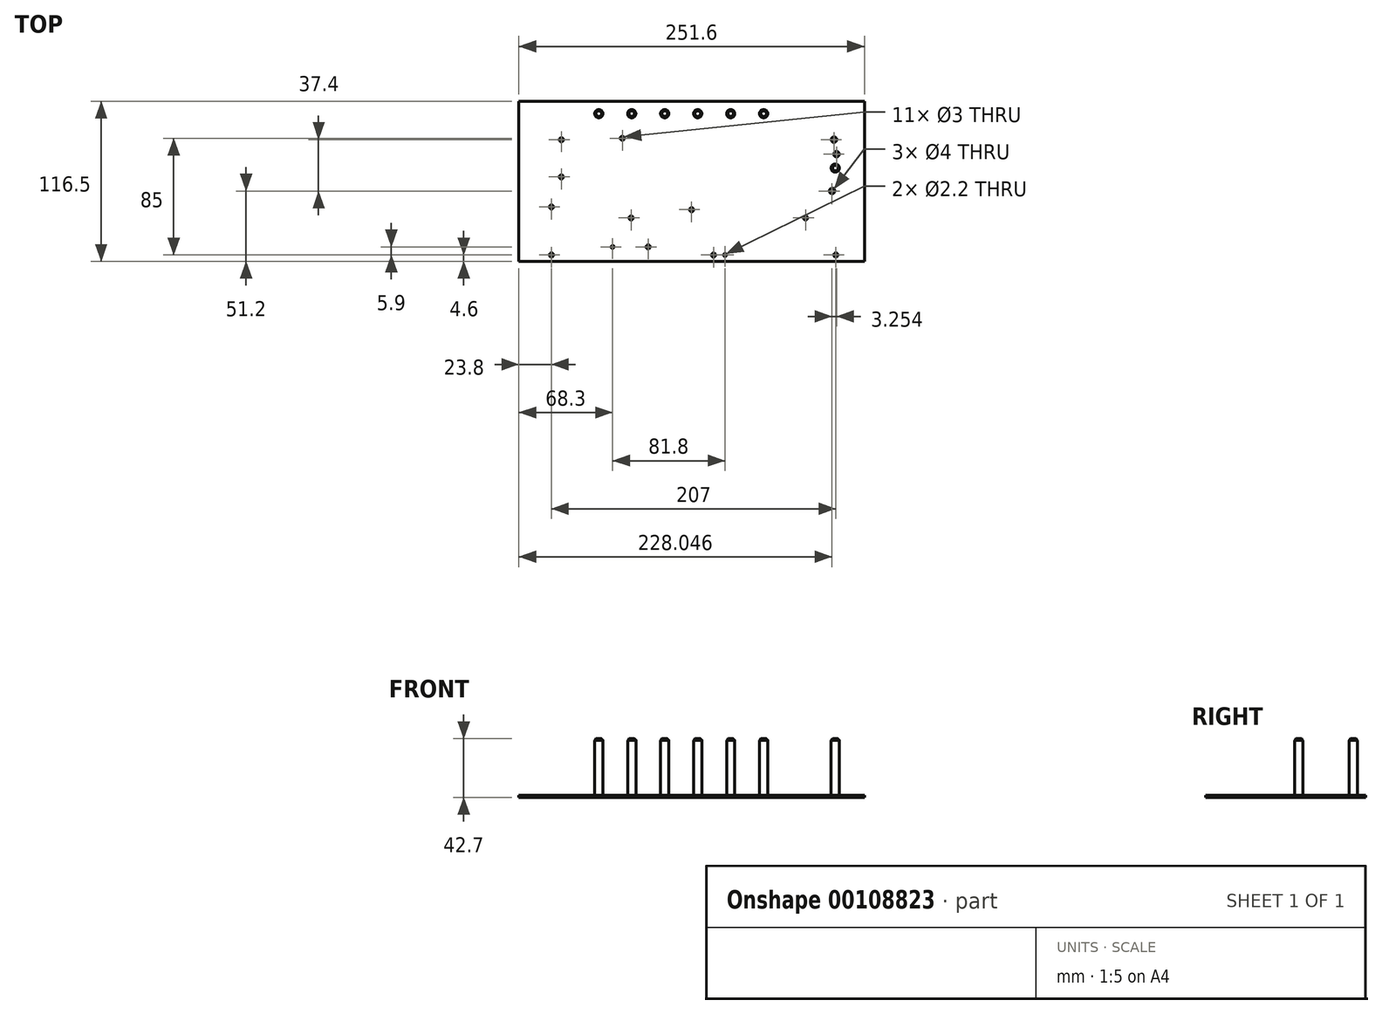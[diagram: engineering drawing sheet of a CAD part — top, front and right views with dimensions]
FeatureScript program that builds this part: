
annotation { "Feature Type Name" : "Feature", "Feature Type Description" : "" }
export const myFeature = defineFeature(function(context is Context, id is Id, definition is map)
    precondition{}
    {
        {
            var Q0;
            Q0=qCreatedBy(makeId("Top.planeOp"),FACE);
            var sketch = newSketch(context, id + "F0", { "sketchPlane" : qUnion([Q0])});
            skLineSegment(sketch, "E0.bottom", {"start": v(0, 0) * mm, "end": v(251.6, 0) * mm});
            skLineSegment(sketch, "E0.top", {"start": v(0, 116.5) * mm, "end": v(251.6, 116.5) * mm});
            skLineSegment(sketch, "E0.left", {"start": v(0, 0) * mm, "end": v(0, 116.5) * mm});
            skLineSegment(sketch, "E0.right", {"start": v(251.6, 0) * mm, "end": v(251.6, 116.5) * mm});
            skLineSegment(sketch, "E1", {"start": v(0, 4.6) * mm, "end": v(251.6, 4.6) * mm, "construction": true});
            skLineSegment(sketch, "E2", {"start": v(23.8, 0) * mm, "end": v(23.8, 116.5) * mm, "construction": true});
            skCircle(sketch, "E3", {"center": v(23.8, 4.6) * mm, "radius": 1.5 * mm});
            skLineSegment(sketch, "E4", {"start": v(0, 39.6) * mm, "end": v(251.6, 39.6) * mm, "construction": true});
            skCircle(sketch, "E5", {"center": v(23.8, 39.6) * mm, "radius": 1.5 * mm});
            skLineSegment(sketch, "E6", {"start": v(0, 31.6) * mm, "end": v(251.6, 31.6) * mm, "construction": true});
            skCircle(sketch, "E7", {"center": v(81.8, 31.6) * mm, "radius": 1.5 * mm});
            skCircle(sketch, "E8", {"center": v(208.8, 31.6) * mm, "radius": 1.5 * mm});
            skCircle(sketch, "E9", {"center": v(141.8, 4.6) * mm, "radius": 1.5 * mm});
            skCircle(sketch, "E10", {"center": v(150.1, 4.6) * mm, "radius": 1.1 * mm});
            skCircle(sketch, "E11", {"center": v(230.8, 4.6) * mm, "radius": 1.5 * mm});
            skCircle(sketch, "E12", {"center": v(125.8, 37.6) * mm, "radius": 1.5 * mm});
            skLineSegment(sketch, "E13", {"start": v(31, 0) * mm, "end": v(31, 116.5) * mm, "construction": true});
            skCircle(sketch, "E14", {"center": v(31, 61.5) * mm, "radius": 1.5 * mm});
            skCircle(sketch, "E15", {"center": v(31, 88.5) * mm, "radius": 1.5 * mm});
            skLineSegment(sketch, "E16", {"start": v(0, 10.5) * mm, "end": v(251.6, 10.5) * mm, "construction": true});
            skCircle(sketch, "E17", {"center": v(68.3, 10.5) * mm, "radius": 1.1 * mm});
            skCircle(sketch, "E18", {"center": v(94.2, 10.5) * mm, "radius": 1.5 * mm});
            skCircle(sketch, "E19", {"center": v(75.4, 89.6) * mm, "radius": 1.5 * mm});
            skCircle(sketch, "E20", {"center": v(228.05, 51.2) * mm, "radius": 2 * mm});
            skCircle(sketch, "E21", {"center": v(231.3, 78) * mm, "radius": 2 * mm});
            skCircle(sketch, "E22", {"center": v(229.5, 88.6) * mm, "radius": 2 * mm});
            skSolve(sketch);
        }
        {
            var Q0;
            Q0=makeQuery(id+"F0.imprint","IMPRINT",FACE,{"disambiguationData":[TD([[makeQuery(id+"F0.imprint","IMPRINT",EDGE,{"derivedFrom":sQuery(id+"F0.wireOp",EDGE,"E0.bottom")}),1.0]])]});
            extrude(context, id + "F1", {"entities" : qUnion([Q0]), "oppositeDirection" : true, "offsetDistance" : 25 * mm, "depth" : 1.6 * mm});
        }
        {
            var Q0;
            Q0=makeQuery(id+"F0.imprint","IMPRINT",FACE,{"disambiguationData":[TD([[makeQuery(id+"F0.imprint","IMPRINT",EDGE,{"derivedFrom":sQuery(id+"F0.wireOp",EDGE,"E0.bottom")}),1.0]])]});
            var sketch = newSketch(context, id + "F2", { "sketchPlane" : qUnion([Q0])});
            skCircle(sketch, "E23", {"center": v(58.25, 107.5) * mm, "radius": 3 * mm});
            skCircle(sketch, "E24.1.0.0", {"center": v(82.25, 107.5) * mm, "radius": 3 * mm});
            skCircle(sketch, "E24.2.0.0", {"center": v(106.25, 107.5) * mm, "radius": 3 * mm});
            skCircle(sketch, "E24.3.0.0", {"center": v(130.25, 107.5) * mm, "radius": 3 * mm});
            skCircle(sketch, "E24.4.0.0", {"center": v(154.25, 107.5) * mm, "radius": 3 * mm});
            skCircle(sketch, "E24.5.0.0", {"center": v(178.25, 107.5) * mm, "radius": 3 * mm});
            skLineSegment(sketch, "E24.direction1", {"start": v(58.25, 107.5) * mm, "end": v(82.25, 107.5) * mm, "construction": true});
            skSolve(sketch);
        }
        {
            var Q0;
            Q0 = qSketchRegion(id + "F2", true);
            extrude(context, id + "F3", {"entities" : qUnion([Q0]), "depth" : 41.1 * mm, "offsetDistance" : 25 * mm});
        }
        {
            var Q0;
            Q0=makeQuery(id+"F3.opExtrude","CAP_EDGE",EDGE,{"disambiguationData":[OSD([sQuery(id+"F2.wireOp",EDGE,"E23")])],"isStart":false});
            var Q1;
            Q1=makeQuery(id+"F3.opExtrude","CAP_EDGE",EDGE,{"disambiguationData":[OSD([sQuery(id+"F2.wireOp",EDGE,"E24.1.0.0")])],"isStart":false});
            var Q2;
            Q2=makeQuery(id+"F3.opExtrude","CAP_EDGE",EDGE,{"disambiguationData":[OSD([sQuery(id+"F2.wireOp",EDGE,"E24.2.0.0")])],"isStart":false});
            var Q3;
            Q3=makeQuery(id+"F3.opExtrude","CAP_EDGE",EDGE,{"disambiguationData":[OSD([sQuery(id+"F2.wireOp",EDGE,"E24.3.0.0")])],"isStart":false});
            var Q4;
            Q4=makeQuery(id+"F3.opExtrude","CAP_EDGE",EDGE,{"disambiguationData":[OSD([sQuery(id+"F2.wireOp",EDGE,"E24.4.0.0")])],"isStart":false});
            var Q5;
            Q5=makeQuery(id+"F3.opExtrude","CAP_EDGE",EDGE,{"disambiguationData":[OSD([sQuery(id+"F2.wireOp",EDGE,"E24.5.0.0")])],"isStart":false});
            chamfer(context, id + "F4", {"entities" : qUnion([Q0, Q1, Q2, Q3, Q4, Q5]), "width" : 1 * mm, "tangentPropagation" : true});
        }
        {
            var Q0;
            Q0=qCreatedBy(makeId("Top.planeOp"),FACE);
            var sketch = newSketch(context, id + "F5", { "sketchPlane" : qUnion([Q0])});
            skCircle(sketch, "E25", {"center": v(230.4, 67.9) * mm, "radius": 3 * mm});
            skSolve(sketch);
        }
        {
            var Q0;
            Q0 = qSketchRegion(id + "F5", true);
            extrude(context, id + "F6", {"entities" : qUnion([Q0]), "depth" : 41.1 * mm, "offsetDistance" : 25 * mm});
        }
        {
            var Q0;
            Q0=makeQuery(id+"F6.opExtrude","CAP_EDGE",EDGE,{"disambiguationData":[OSD([sQuery(id+"F5.wireOp",EDGE,"E25")])],"isStart":false});
            chamfer(context, id + "F7", {"entities" : qUnion([Q0]), "width" : 1 * mm, "tangentPropagation" : true});
        }
    });
